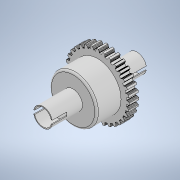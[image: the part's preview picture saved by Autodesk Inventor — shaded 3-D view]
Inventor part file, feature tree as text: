
AUTODESK INVENTOR PART (.ipt)
format: ipt  version: 2020 (Build 240168000, 168)  size: 938,496 bytes
history: native  units: mm
features: sketch x5, extrude x4, other x3, projected_geometry x2, hole x1, mirror x1, fillet x1
ambient origin geometry x8: Origin, YZ Plane, XZ Plane, XY Plane, X Axis, Y Axis, Z Axis, Center Point
bodies: Body1 (feature_tree)
feature tree (17):
  other  "Дифференциал"
  other  "Твердое тело1"
  extrude  "Выдавливание1"  Depth=5.0mm TaperAngle=0.0deg
  extrude  "Выдавливание2"  Depth=25.0mm
  extrude  "Выдавливание3"  Depth=13.0mm TaperAngle=0.0deg
  hole  "Отверстие1"  [1 undecoded]
  extrude  "Выдавливание4"  Depth=16.0mm TaperAngle=0.0deg
  other  "РабПлоскость1"
  mirror  "Зеркальное отражение1"
  fillet  "Сопряжение1"  Radius=2.0mm
  sketch  "Эскиз1"
  sketch  "Эскиз2"
  sketch  "Эскиз4"
  projected_geometry  "Спроецированная петля1"
  sketch  "Эскиз5"
  projected_geometry  "Спроецированная петля2"
  sketch  "Эскиз6"
note: 1 required parameter value undecoded (feature->parameter linkage not recoverable at this tier; creation-order binding heuristic only, values carry confidence <= 0.55)
